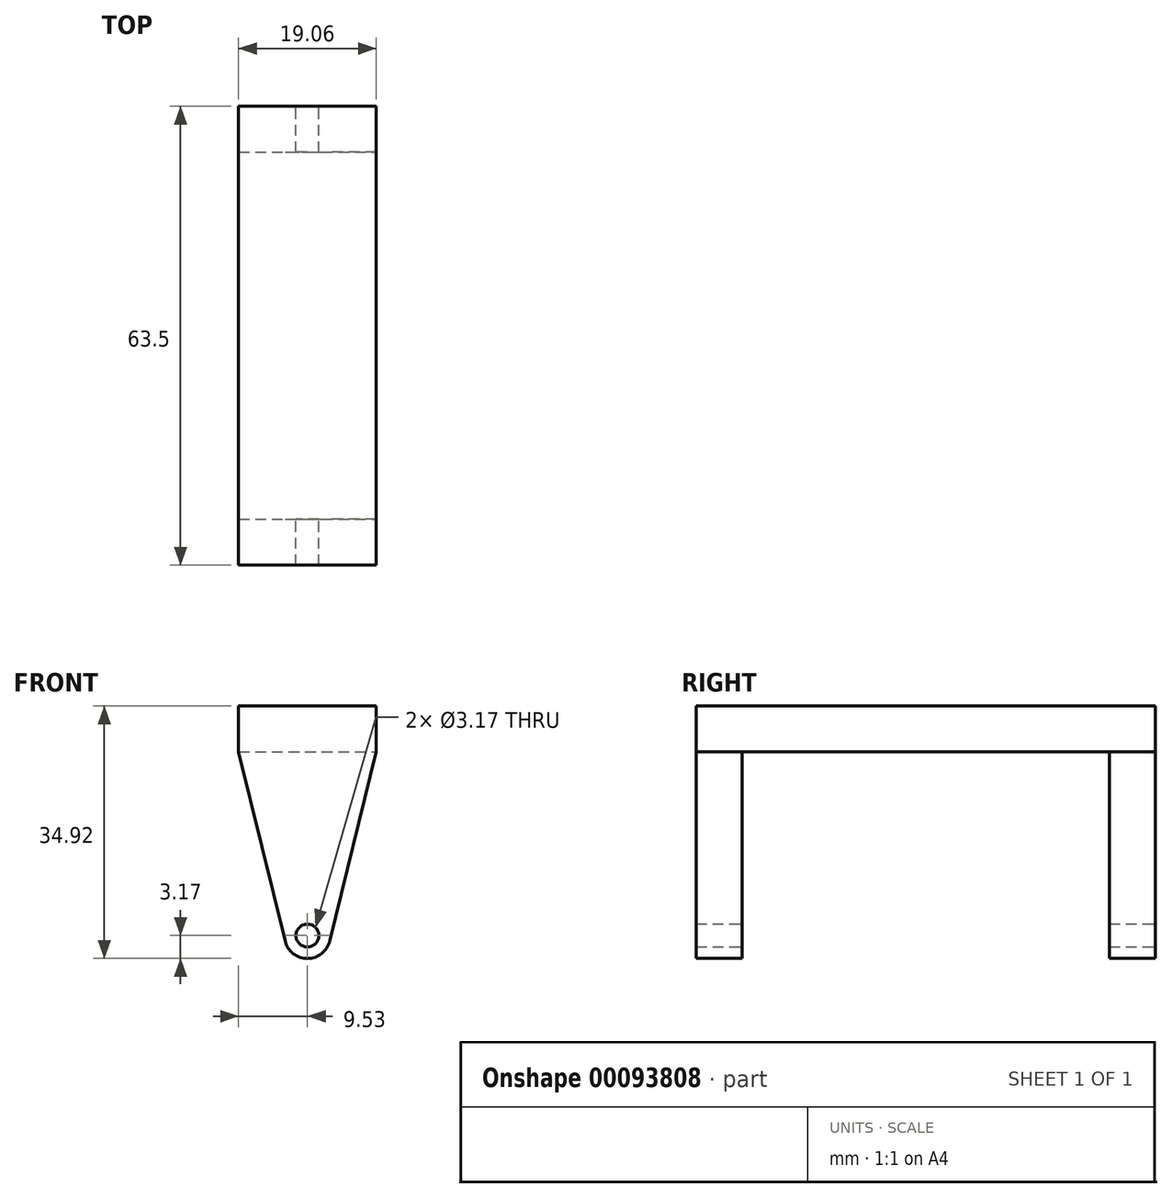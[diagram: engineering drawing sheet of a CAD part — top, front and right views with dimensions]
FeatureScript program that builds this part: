
annotation { "Feature Type Name" : "Feature", "Feature Type Description" : "" }
export const myFeature = defineFeature(function(context is Context, id is Id, definition is map)
    precondition{}
    {
        {
            var Q0;
            Q0=qCreatedBy(makeId("Front.planeOp"),FACE);
            var sketch = newSketch(context, id + "F0", { "sketchPlane" : qUnion([Q0])});
            skLineSegment(sketch, "E0", {"start": v(-9.52, 0) * mm, "end": v(-3.08, -26.16) * mm});
            skLineSegment(sketch, "E1", {"start": v(9.52, 0) * mm, "end": v(3.08, -26.16) * mm});
            skArc(sketch, "E2", {"start": v(-3.08, -26.16) * mm, "mid": v(0, -28.58) * mm, "end": v(3.08, -26.16) * mm});
            skLineSegment(sketch, "E3", {"start": v(-9.53, 0) * mm, "end": v(-9.53, 6.35) * mm});
            skLineSegment(sketch, "E4", {"start": v(-9.53, 6.35) * mm, "end": v(9.53, 6.35) * mm});
            skLineSegment(sketch, "E5", {"start": v(9.52, 6.35) * mm, "end": v(9.53, 0) * mm});
            skSolve(sketch);
        }
        {
            var Q0;
            Q0 = qSketchRegion(id + "F0", true);
            extrude(context, id + "F1", {"entities" : qUnion([Q0]), "depth" : 63.5 * mm});
        }
        {
            var Q0;
            Q0=makeQuery(id+"F1.opExtrude","SWEPT_FACE",FACE,{"disambiguationData":[OSD([sQuery(id+"F0.wireOp",EDGE,"E5")])]});
            var sketch = newSketch(context, id + "F2", { "sketchPlane" : qUnion([Q0])});
            skLineSegment(sketch, "E6.bottom", {"start": v(-57.15, 0) * mm, "end": v(-6.35, 0) * mm});
            skLineSegment(sketch, "E6.top", {"start": v(-57.15, -35) * mm, "end": v(-6.35, -35) * mm});
            skLineSegment(sketch, "E6.left", {"start": v(-57.15, 0) * mm, "end": v(-57.15, -35) * mm});
            skLineSegment(sketch, "E6.right", {"start": v(-6.35, 0) * mm, "end": v(-6.35, -35) * mm});
            skSolve(sketch);
        }
        {
            var Q0;
            Q0 = qSketchRegion(id + "F2", true);
            extrude(context, id + "F3", {"entities" : qUnion([Q0]), "operationType" : NewBodyOperationType.REMOVE, "endBound" : BoundingType.THROUGH_ALL, "oppositeDirection" : true, "depth" : 25.4 * mm});
        }
        {
            var Q0;
            Q0=makeQuery(id+"F1.opExtrude","CAP_FACE",FACE,{"disambiguationData":[OSD([sQuery(id+"F0.wireOp",EDGE,"E0"),sQuery(id+"F0.wireOp",EDGE,"E1"),sQuery(id+"F0.wireOp",EDGE,"E2"),sQuery(id+"F0.wireOp",EDGE,"E3"),sQuery(id+"F0.wireOp",EDGE,"E4"),sQuery(id+"F0.wireOp",EDGE,"E5")])],"isStart":true});
            var sketch = newSketch(context, id + "F4", { "sketchPlane" : qUnion([Q0])});
            skCircle(sketch, "E7", {"center": v(0, -25.4) * mm, "radius": 1.59 * mm});
            skSolve(sketch);
        }
        {
            var Q0;
            Q0 = qSketchRegion(id + "F4", true);
            extrude(context, id + "F5", {"entities" : qUnion([Q0]), "operationType" : NewBodyOperationType.REMOVE, "endBound" : BoundingType.THROUGH_ALL, "oppositeDirection" : true, "depth" : 25.4 * mm});
        }
    });
